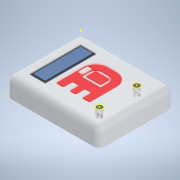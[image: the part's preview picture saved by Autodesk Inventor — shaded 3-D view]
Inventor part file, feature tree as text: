
AUTODESK INVENTOR PART (.ipt)
format: ipt  version: 2020 (Build 240168000, 168)  size: 348,160 bytes
history: native  units: in
note: dims shown in document units (in); Inventor stores cm internally (conversion verified against a paired STEP export)
features: sketch x9, extrude x6, fillet x5, projected_geometry x1
ambient origin geometry x8: Origin, YZ Plane, XZ Plane, XY Plane, X Axis, Y Axis, Z Axis, Center Point
bodies: Solid1 (feature_tree)
feature tree (21):
  extrude  "Extrusion1"  Depth=120.0in
  extrude  "Extrusion2"  Depth=82.0in
  sketch  "Sketch3"  dims[d6=19.0in d7=19.0in d8=25.0in d9=2.0in d10=0.0in]
  extrude  "Extrusion3"  Depth=19.0in
  fillet  "Fillet1"  Radius=25.0in
  fillet  "Fillet2"  Radius=2.0in
  extrude  "Extrusion4"  Depth=2.0in
  extrude  "Extrusion5"  Depth=2.0in
  sketch  "Sketch7"  dims[d21=20.0in]
  extrude  "Extrusion6"  Depth=10.0in
  fillet  "Fillet3"  Radius=10.0in
  fillet  "Fillet4"  Radius=10.0in
  fillet  "Fillet5"  Radius=20.0in
  sketch  "Sketch10"  dims[d23=10.0in d24=0.0in d25=2.0in d26=2.0in d27=1.0in d28=1.0in d29=1.0in d30=1.0in d31=2.0in d32=2.0in d33=4.0in d34=0.0in d35=64.0in d36=54.0in d37=28.0in d38=8.0in d39=12.0in d40=12.0in d41=10.0in d42=10.0in d43=15.0in d44=15.0in d45=12.0in d46=15.0in d47=3.0in d48=3.0in d49=3.0in d50=3.0in d51=2.0in d52=2.0in d53=2.0in d54=0.0in d55=20.0in d56=10.0in d57=2.0in]
  sketch  "Sketch1"  dims[d0=150.0in d1=120.0in]
  sketch  "Sketch2"  dims[d2=30.0in d3=0.0in d5=82.0in]
  sketch  "Sketch4"  dims[d11=2.0in d12=2.0in]
  sketch  "Sketch5"  dims[d13=2.0in d14=2.0in]
  sketch  "Sketch6"  dims[d15=2.0in d16=0.0in d17=10.0in d18=10.0in d19=10.0in d20=20.0in]
  projected_geometry  "Projected Loop1"
  sketch  "Sketch9"  dims[d22=20.0in]
